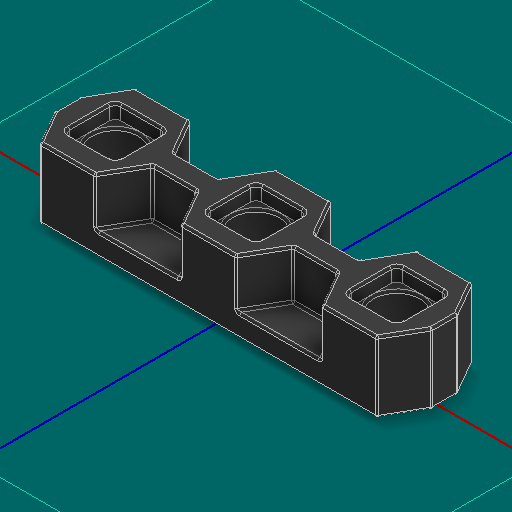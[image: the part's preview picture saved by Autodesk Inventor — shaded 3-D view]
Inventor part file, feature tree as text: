
AUTODESK INVENTOR PART (.ipt)
format: ipt  version: 2025 (Build 290162000, 162)  size: 503,808 bytes
history: native  units: in
note: dims shown in document units (in); Inventor stores cm internally (conversion verified against a paired STEP export)
features: other x3, sketch x1
ambient origin geometry x8: Origin, YZ Plane, XZ Plane, XY Plane, X Axis, Y Axis, Z Axis, Center Point
bodies: Solid1 (feature_tree)
feature tree (4):
  other  "Bearing Flat Low Profile.ipt"
  other  "Solid1::Bearing Flat Low Profile.ipt"
  other  "TaggingFeature1"
  sketch  "Sketch1"  dims[d0=0.3937in]
